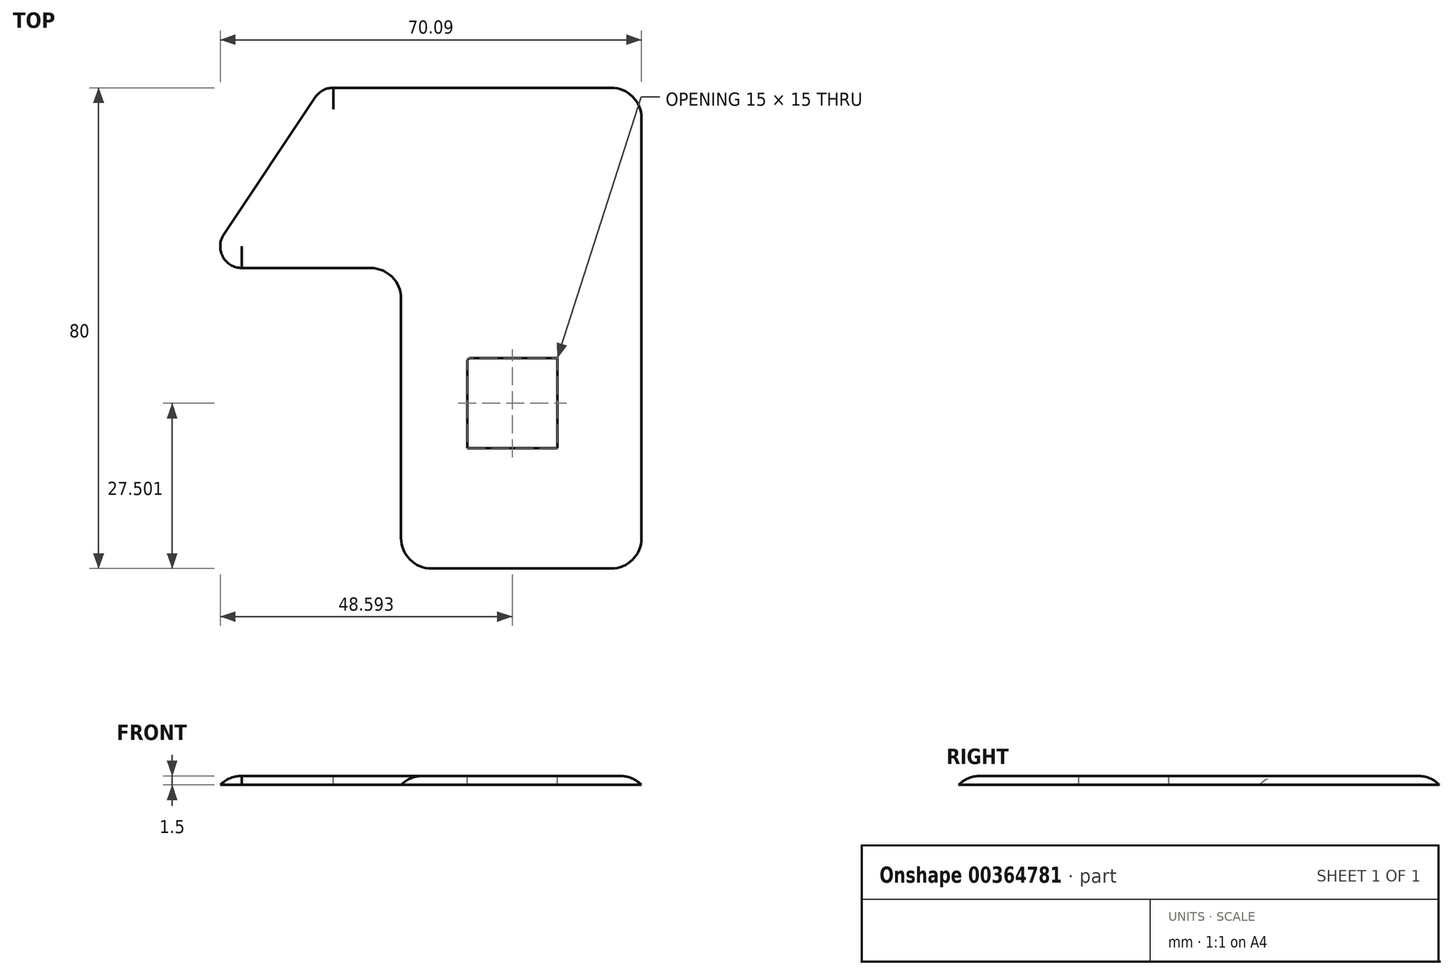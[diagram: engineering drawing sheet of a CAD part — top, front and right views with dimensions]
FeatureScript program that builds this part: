
annotation { "Feature Type Name" : "Feature", "Feature Type Description" : "" }
export const myFeature = defineFeature(function(context is Context, id is Id, definition is map)
    precondition{}
    {
        {
            var Q0;
            Q0=qCreatedBy(makeId("Top.planeOp"),FACE);
            var sketch = newSketch(context, id + "F0", { "sketchPlane" : qUnion([Q0])});
            skLineSegment(sketch, "E0", {"start": v(64.21, 53.26) * mm, "end": v(64.21, -26.74) * mm});
            skLineSegment(sketch, "E1", {"start": v(64.21, -26.74) * mm, "end": v(24.21, -26.74) * mm});
            skLineSegment(sketch, "E2", {"start": v(24.21, -26.74) * mm, "end": v(24.21, 23.26) * mm});
            skLineSegment(sketch, "E3", {"start": v(24.21, 23.26) * mm, "end": v(-10.79, 23.26) * mm});
            skLineSegment(sketch, "E4", {"start": v(-10.79, 23.26) * mm, "end": v(9.21, 53.26) * mm});
            skLineSegment(sketch, "E5", {"start": v(9.21, 53.26) * mm, "end": v(64.21, 53.26) * mm});
            skSolve(sketch);
        }
        {
            var Q0;
            Q0=makeQuery(id+"F0.imprint","IMPRINT",FACE,{"disambiguationData":[TD([[makeQuery(id+"F0.imprint","IMPRINT",EDGE,{"derivedFrom":sQuery(id+"F0.wireOp",EDGE,"E0")}),-1.0]])]});
            extrude(context, id + "F1", {"entities" : qUnion([Q0]), "depth" : 1.5 * mm});
        }
        {
            var Q0;
            Q0=makeQuery(id+"F1.opExtrude","CAP_FACE",FACE,{"disambiguationData":[OSD([sQuery(id+"F0.wireOp",EDGE,"E0"),sQuery(id+"F0.wireOp",EDGE,"E1"),sQuery(id+"F0.wireOp",EDGE,"E2"),sQuery(id+"F0.wireOp",EDGE,"E3"),sQuery(id+"F0.wireOp",EDGE,"E4"),sQuery(id+"F0.wireOp",EDGE,"E5")])],"isStart":false});
            var sketch = newSketch(context, id + "F2", { "sketchPlane" : qUnion([Q0])});
            skLineSegment(sketch, "E6", {"start": v(50.21, -6.74) * mm, "end": v(35.21, -6.74) * mm});
            skLineSegment(sketch, "E7", {"start": v(35.21, -6.74) * mm, "end": v(35.21, 8.26) * mm});
            skLineSegment(sketch, "E8", {"start": v(35.21, 8.26) * mm, "end": v(50.21, 8.26) * mm});
            skLineSegment(sketch, "E9", {"start": v(35.21, 8.26) * mm, "end": v(35.21, 53.26) * mm, "construction": true});
            skLineSegment(sketch, "E10", {"start": v(64.21, 53.26) * mm, "end": v(50.21, 53.26) * mm, "construction": true});
            skLineSegment(sketch, "E11", {"start": v(50.21, 53.26) * mm, "end": v(50.21, 8.26) * mm, "construction": true});
            skLineSegment(sketch, "E12", {"start": v(50.21, 8.26) * mm, "end": v(50.21, -6.74) * mm});
            skLineSegment(sketch, "E13", {"start": v(50.21, 8.26) * mm, "end": v(40.21, 8.26) * mm});
            skLineSegment(sketch, "E14", {"start": v(40.21, 8.26) * mm, "end": v(40.21, 31.26) * mm});
            skLineSegment(sketch, "E15", {"start": v(40.21, 31.26) * mm, "end": v(50.21, 31.26) * mm});
            skLineSegment(sketch, "E16", {"start": v(50.21, 31.26) * mm, "end": v(50.21, 8.26) * mm});
            skSolve(sketch);
        }
        {
            var Q0;
            Q0=makeQuery(id+"F2.imprint","IMPRINT",FACE,{"disambiguationData":[TD([[makeQuery(id+"F2.imprint","IMPRINT",EDGE,{"derivedFrom":sQuery(id+"F2.wireOp",EDGE,"E6")}),-1.0]])]});
            var Q1;
            Q1=makeQuery(id+"F2.imprint","IMPRINT",FACE,{"disambiguationData":[TD([[makeQuery(id+"F2.imprint","IMPRINT",EDGE,{"derivedFrom":sQuery(id+"F2.wireOp",EDGE,"E13")}),-1.0]])]});
            extrude(context, id + "F3", {"entities" : qUnion([Q0, Q1]), "operationType" : NewBodyOperationType.REMOVE, "oppositeDirection" : true, "depth" : 1.5 * mm});
        }
        {
            var Q0;
            Q0=makeQuery(id+"F1.opExtrude","SWEPT_EDGE",EDGE,{"disambiguationData":[OSD([sQuery(id+"F0.wireOp",EDGE,"E0"),sQuery(id+"F0.wireOp",EDGE,"E5")])]});
            var Q1;
            Q1=makeQuery(id+"F1.opExtrude","SWEPT_EDGE",EDGE,{"disambiguationData":[OSD([sQuery(id+"F0.wireOp",EDGE,"E0"),sQuery(id+"F0.wireOp",EDGE,"E1")])]});
            var Q2;
            Q2=makeQuery(id+"F1.opExtrude","SWEPT_EDGE",EDGE,{"disambiguationData":[OSD([sQuery(id+"F0.wireOp",EDGE,"E1"),sQuery(id+"F0.wireOp",EDGE,"E2")])]});
            var Q3;
            Q3=makeQuery(id+"F1.opExtrude","SWEPT_EDGE",EDGE,{"disambiguationData":[OSD([sQuery(id+"F0.wireOp",EDGE,"E2"),sQuery(id+"F0.wireOp",EDGE,"E3")])]});
            fillet(context, id + "F4", {"entities" : qUnion([Q0, Q1, Q2, Q3]), "radius" : 5.08 * mm, "tangentPropagation" : true, "allowEdgeOverflow" : false});
        }
        {
            var Q0;
            Q0=makeQuery(id+"F1.opExtrude","CAP_EDGE",EDGE,{"disambiguationData":[OSD([sQuery(id+"F0.wireOp",EDGE,"E3")])],"isStart":false});
            fillet(context, id + "F5", {"entities" : qUnion([Q0]), "radius" : 5.08 * mm, "tangentPropagation" : true, "allowEdgeOverflow" : false});
        }
        {
            var Q0;
            Q0=makeQuery(id+"F1.opExtrude","CAP_EDGE",EDGE,{"disambiguationData":[OSD([sQuery(id+"F0.wireOp",EDGE,"E4")])],"isStart":false});
            fillet(context, id + "F6", {"entities" : qUnion([Q0]), "radius" : 5.08 * mm, "tangentPropagation" : true, "allowEdgeOverflow" : false});
        }
        {
            var Q0;
            Q0=makeQuery(id+"F3.boolean.opBoolean","COPY",EDGE,{"derivedFrom":makeQuery(id+"F3.opExtrude","CAP_EDGE",EDGE,{"disambiguationData":[OSD([sQuery(id+"F2.wireOp",EDGE,"E15")])],"isStart":true})});
            var Q1;
            Q1=makeQuery(id+"F3.boolean.opBoolean","COPY",EDGE,{"derivedFrom":makeQuery(id+"F3.opExtrude","CAP_EDGE",EDGE,{"disambiguationData":[OSD([sQuery(id+"F2.wireOp",EDGE,"E12"),sQuery(id+"F2.wireOp",EDGE,"E16")])],"isStart":true})});
            var Q2;
            Q2=makeQuery(id+"F3.boolean.opBoolean","COPY",EDGE,{"derivedFrom":makeQuery(id+"F3.opExtrude","CAP_EDGE",EDGE,{"disambiguationData":[OSD([sQuery(id+"F2.wireOp",EDGE,"E14")])],"isStart":true})});
            var Q3;
            Q3=makeQuery(id+"F3.boolean.opBoolean","COPY",EDGE,{"derivedFrom":makeQuery(id+"F3.opExtrude","CAP_EDGE",EDGE,{"disambiguationData":[OSD([sQuery(id+"F2.wireOp",EDGE,"E8")])],"isStart":true})});
            var Q4;
            Q4=makeQuery(id+"F3.boolean.opBoolean","COPY",EDGE,{"derivedFrom":makeQuery(id+"F3.opExtrude","SWEPT_EDGE",EDGE,{"disambiguationData":[OSD([sQuery(id+"F2.wireOp",EDGE,"E8"),sQuery(id+"F2.wireOp",EDGE,"E13"),sQuery(id+"F2.wireOp",EDGE,"E14")])]})});
            var Q5;
            Q5=makeQuery(id+"F3.boolean.opBoolean","COPY",EDGE,{"derivedFrom":makeQuery(id+"F3.opExtrude","CAP_EDGE",EDGE,{"disambiguationData":[OSD([sQuery(id+"F2.wireOp",EDGE,"E7")])],"isStart":true})});
            var Q6;
            Q6=makeQuery(id+"F3.boolean.opBoolean","COPY",EDGE,{"derivedFrom":makeQuery(id+"F3.opExtrude","CAP_EDGE",EDGE,{"disambiguationData":[OSD([sQuery(id+"F2.wireOp",EDGE,"E6")])],"isStart":true})});
            fillet(context, id + "F7", {"entities" : qUnion([Q0, Q1, Q2, Q3, Q4, Q5, Q6]), "radius" : 0.5 * mm, "tangentPropagation" : true, "allowEdgeOverflow" : false});
        }
    });
